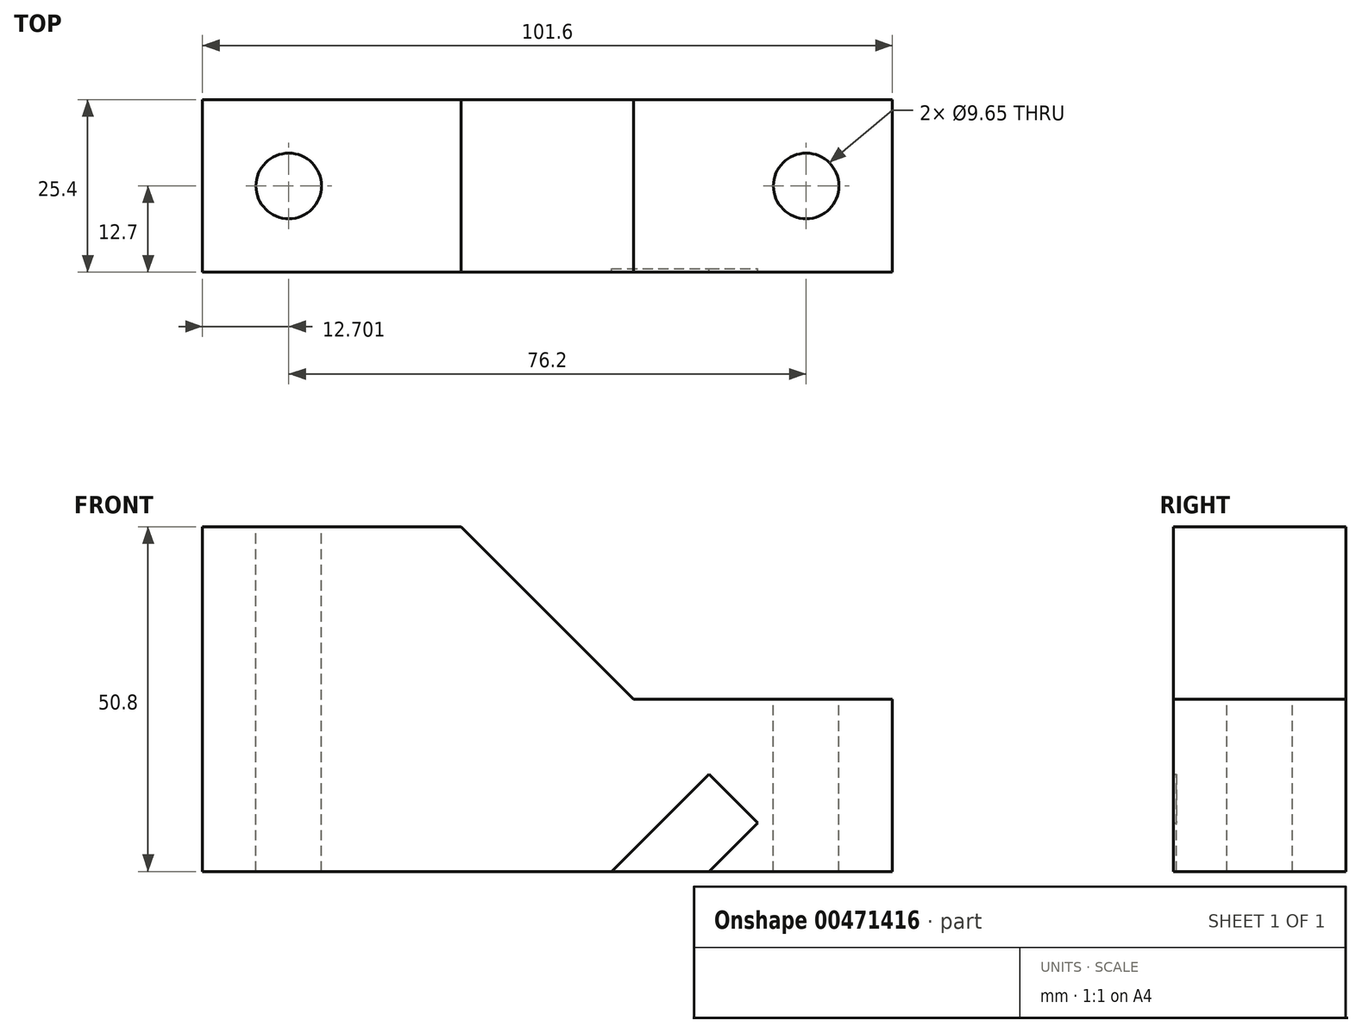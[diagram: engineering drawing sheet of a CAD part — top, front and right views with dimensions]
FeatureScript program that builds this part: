
annotation { "Feature Type Name" : "Feature", "Feature Type Description" : "" }
export const myFeature = defineFeature(function(context is Context, id is Id, definition is map)
    precondition{}
    {
        {
            var Q0;
            Q0=qCreatedBy(makeId("Front.planeOp"),FACE);
            var sketch = newSketch(context, id + "F0", { "sketchPlane" : qUnion([Q0])});
            skLineSegment(sketch, "E0", {"start": v(-60.13, 40.13) * mm, "end": v(-60.13, -10.67) * mm});
            skLineSegment(sketch, "E1", {"start": v(-60.13, -10.67) * mm, "end": v(41.47, -10.67) * mm});
            skLineSegment(sketch, "E2", {"start": v(41.47, -10.67) * mm, "end": v(41.47, 14.73) * mm});
            skLineSegment(sketch, "E3", {"start": v(41.47, 14.73) * mm, "end": v(3.37, 14.73) * mm});
            skLineSegment(sketch, "E4", {"start": v(3.37, 14.73) * mm, "end": v(-22.03, 40.13) * mm});
            skLineSegment(sketch, "E5", {"start": v(-22.03, 40.13) * mm, "end": v(-60.13, 40.13) * mm});
            skSolve(sketch);
        }
        {
            var Q0;
            Q0 = qSketchRegion(id + "F0", true);
            extrude(context, id + "F1", {"entities" : qUnion([Q0]), "depth" : 25.4 * mm});
        }
        {
            var Q0;
            Q0=makeQuery(id+"F1.opExtrude","SWEPT_FACE",FACE,{"disambiguationData":[OSD([sQuery(id+"F0.wireOp",EDGE,"E5")])]});
            var sketch = newSketch(context, id + "F2", { "sketchPlane" : qUnion([Q0])});
            skCircle(sketch, "E6", {"center": v(-47.43, -12.7) * mm, "radius": 4.83 * mm});
            skCircle(sketch, "E7", {"center": v(28.77, -12.7) * mm, "radius": 4.83 * mm});
            skSolve(sketch);
        }
        {
            var Q0;
            Q0=makeQuery(id+"F2.imprint","IMPRINT",FACE,{"disambiguationData":[TD([[makeQuery(id+"F2.imprint","IMPRINT",EDGE,{"derivedFrom":sQuery(id+"F2.wireOp",EDGE,"E6")}),1.0]])]});
            var Q1;
            Q1=makeQuery(id+"F2.imprint","IMPRINT",FACE,{"disambiguationData":[TD([[makeQuery(id+"F2.imprint","IMPRINT",EDGE,{"derivedFrom":sQuery(id+"F2.wireOp",EDGE,"E7")}),1.0]])]});
            extrude(context, id + "F3", {"entities" : qUnion([Q0, Q1]), "operationType" : NewBodyOperationType.REMOVE, "endBound" : BoundingType.THROUGH_ALL, "oppositeDirection" : true, "depth" : 25.4 * mm});
        }
        {
            var Q0;
            Q0=makeQuery(id+"F1.opExtrude","SWEPT_FACE",FACE,{"disambiguationData":[OSD([sQuery(id+"F0.wireOp",EDGE,"E4")])]});
            var sketch = newSketch(context, id + "F4", { "sketchPlane" : qUnion([Q0])});
            skLineSegment(sketch, "E8.bottom", {"start": v(-32.52, -7.62) * mm, "end": v(-24.9, -7.62) * mm});
            skLineSegment(sketch, "E8.top", {"start": v(-32.52, -17.78) * mm, "end": v(-24.9, -17.78) * mm});
            skLineSegment(sketch, "E8.left", {"start": v(-32.52, -7.62) * mm, "end": v(-32.52, -17.78) * mm});
            skLineSegment(sketch, "E8.right", {"start": v(-24.9, -7.62) * mm, "end": v(-24.9, -17.78) * mm});
            skPoint(sketch, "E8.middle", {"position": v(-28.71, -12.7) * mm});
            skSolve(sketch);
        }
        {
            var Q0;
            Q0=makeQuery(id+"F4.imprint","IMPRINT",FACE,{"disambiguationData":[TD([[makeQuery(id+"F4.imprint","IMPRINT",EDGE,{"derivedFrom":sQuery(id+"F4.wireOp",EDGE,"E8.bottom")}),-1.0]])]});
            extrude(context, id + "F5", {"entities" : qUnion([Q0]), "operationType" : NewBodyOperationType.REMOVE, "endBound" : BoundingType.THROUGH_ALL, "oppositeDirection" : true, "depth" : 25.4 * mm});
        }
    });
